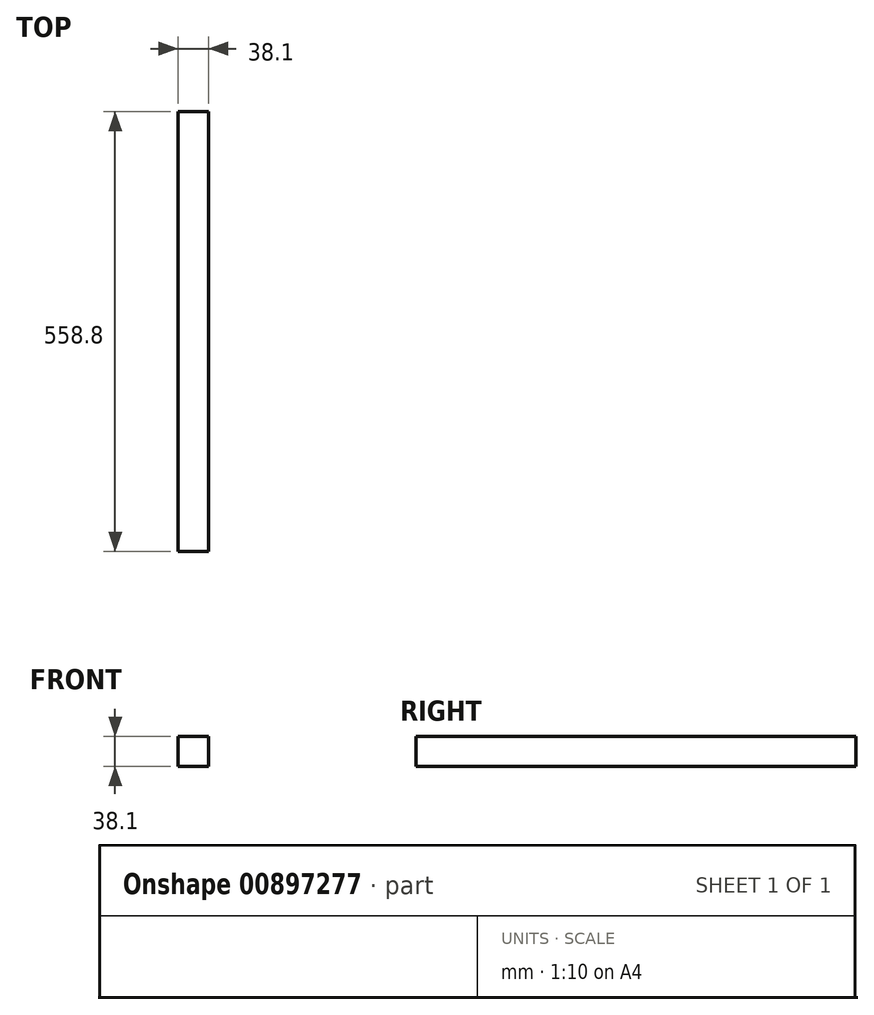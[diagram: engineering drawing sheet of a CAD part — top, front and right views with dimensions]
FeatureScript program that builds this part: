
annotation { "Feature Type Name" : "Feature", "Feature Type Description" : "" }
export const myFeature = defineFeature(function(context is Context, id is Id, definition is map)
    precondition{}
    {
        {
            var Q0;
            Q0=qCreatedBy(makeId("Front.planeOp"),FACE);
            var sketch = newSketch(context, id + "F0", { "sketchPlane" : qUnion([Q0])});
            skLineSegment(sketch, "E0.bottom", {"start": v(-19.05, 19.05) * mm, "end": v(19.05, 19.05) * mm});
            skLineSegment(sketch, "E0.top", {"start": v(-19.05, -19.05) * mm, "end": v(19.05, -19.05) * mm});
            skLineSegment(sketch, "E0.left", {"start": v(-19.05, 19.05) * mm, "end": v(-19.05, -19.05) * mm});
            skLineSegment(sketch, "E0.right", {"start": v(19.05, 19.05) * mm, "end": v(19.05, -19.05) * mm});
            skPoint(sketch, "E0.middle", {"position": v(0, 0) * mm});
            skSolve(sketch);
        }
        {
            var Q0;
            Q0=makeQuery(id+"F0.imprint","IMPRINT",FACE,{"disambiguationData":[TD([[makeQuery(id+"F0.imprint","IMPRINT",EDGE,{"derivedFrom":sQuery(id+"F0.wireOp",EDGE,"E0.bottom")}),-1.0]])]});
            extrude(context, id + "F1", {"entities" : qUnion([Q0]), "depth" : 558.8 * mm, "offsetDistance" : 25.4 * mm});
        }
    });
